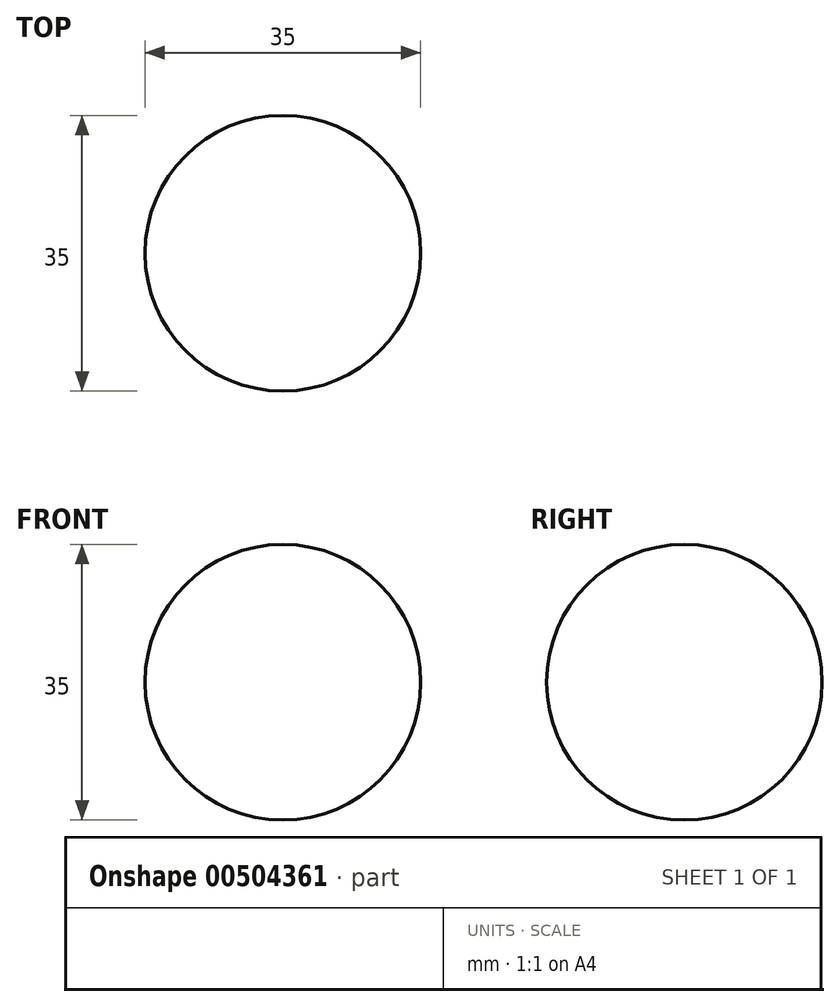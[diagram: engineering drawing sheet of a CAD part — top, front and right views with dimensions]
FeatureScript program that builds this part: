
annotation { "Feature Type Name" : "Feature", "Feature Type Description" : "" }
export const myFeature = defineFeature(function(context is Context, id is Id, definition is map)
    precondition{}
    {
        {
            var Q0;
            Q0=qCreatedBy(makeId("Front.planeOp"),FACE);
            var sketch = newSketch(context, id + "F0", { "sketchPlane" : qUnion([Q0])});
            skArc(sketch, "E0", {"start": v(0, -17.5) * mm, "mid": v(17.5, 0) * mm, "end": v(0, 17.5) * mm});
            skLineSegment(sketch, "E1", {"start": v(0, 17.5) * mm, "end": v(0, -17.5) * mm});
            skSolve(sketch);
        }
        {
            var Q0;
            Q0=makeQuery(id+"F0.imprint","IMPRINT",FACE,{"disambiguationData":[TD([[makeQuery(id+"F0.imprint","IMPRINT",EDGE,{"derivedFrom":sQuery(id+"F0.wireOp",EDGE,"E0")}),1.0]])]});
            var Q1;
            Q1=sQuery(id+"F0.wireOp",EDGE,"E1");
            revolve(context, id + "F1", {"entities" : qUnion([Q0]), "axis" : qUnion([Q1]), "revolveType" : RevolveType.FULL});
        }
    });
